# Revit family: Rohrschelle Maxima PSM, M10-M12, Ø 65-117, Gummi
name_source: partatom
category: HLS-Bauteile
revit_build: Autodesk Revit 2017 (Build: 20190507_1515(x64)
units: mm (PartAtom-declared; Revit-internal decimal feet)

## family parameters
Arbeitsebenenbasiert = Ja
Beim Laden mit Abzugskörper schneiden = Nein
Bemaßung runder Anschluss = Durchmesser verwenden
Gemeinsam genutzt = Ja
Immer vertikal = Nein
Raumberechnungspunkt = Nein
Teiletyp = Normal

## types (7) — shared parameters
A = 31 mm  [stored 0.101706 ft]
Anschluss = M10/M12
Anschlußhöhe = 30 mm
Bauart = zweiteilig
Baustoffklasse = B2
Brandschutz = RAL-GZ 656
DF1 = 26 mm  [stored 0.0853018 ft]
DF2 = 28 mm  [stored 0.0918635 ft]
DS = 6 mm  [stored 0.019685 ft]
DVS = 15 mm  [stored 0.0492126 ft]
Dämmstärke = 6 mm  [stored 0.019685 ft]
Fabrikat = MEFA
Farbe Schalldämmeinlage = schwarz
Firma = MEFA Befestigungs- und Montagesysteme GmbH
HGA = 22 mm  [stored 0.0721785 ft]
Kurztext1 = Rohrschelle Maxima PSM 30x3,0
MB = 30 mm  [stored 0.0984252 ft]
MD = 3 mm  [stored 0.00984252 ft]
Material = Stahl
Material Schalldämmeinlage = TPE
Materialmaße = 30x3,0 mm
Materialname = S235
Mengeneinheit = St
Oberflaeche = galvanisch verzinkt
Schalldämmeinlage = Gummi
Verschluss-Schraube = M8
Vorgabe-Ansicht = 1219 mm
max. Temperaturbeständigkeit = 100 °C
max. zul. Last = 1.70 kN
max. zul. Last horizontal = 0.00 kN
max. zul. Last vertikal = 0.00 kN
zero-valued in all types: Nennweite DN Rohr, Rohraußendurchmesser, Stärke Material

## per-type parameters (varying)
| type | AB | Achsabstand | Artikelnummer | B | Breite | D | D0 | Dmax | Dmin | EAN | Gewicht | Gewicht pro Bauteil | H | Kurztext2 | R | RM | Rohraußendurchmesser Zoll | S | Verschluss | max. Höhe | max. Rohraußendurchmesser | min. Rohraußendurchmesser | vpe |
| Maxima PSM, M10/M12, Ø 65- 70, Gummi | 5 mm  [stored 0.0164042 ft] | 116 mm | 008007501 | 142 mm | 142 mm | 70 mm  [stored 0.229659 ft] | 82 mm  [stored 0.269029 ft] | 70 mm  [stored 0.229659 ft] | 65 mm  [stored 0.213255 ft] | 4250928454812 | 0.38 kg | 0.38 kg | 110 mm | 65 - 70 mm M10/M12 TPE | 41 mm  [stored 0.134514 ft] | 44 mm |  | 116 mm | Pendelsteckmutter | 109 mm  [stored 0.357612 ft] | 70 mm  [stored 0.229659 ft] | 65 mm  [stored 0.213255 ft] | St |
| Maxima PSM, M10/M12, Ø 72- 78, Gummi | 6 mm  [stored 0.019685 ft] | 124 mm | 008010601 | 150 mm | 150 mm | 78 mm  [stored 0.255906 ft] | 90 mm  [stored 0.295276 ft] | 78 mm  [stored 0.255906 ft] | 72 mm  [stored 0.23622 ft] | 4250928454829 | 0.40 kg | 0.40 kg | 118 mm  [stored 0.387139 ft] | 72 - 78 mm M10/M12 TPE | 45 mm  [stored 0.147638 ft] | 48 mm  [stored 0.15748 ft] | 2 1/2 Zoll | 124 mm | Pendelsteckmuttern | 117 mm  [stored 0.383858 ft] | 78 mm  [stored 0.255906 ft] | 72 mm  [stored 0.23622 ft] | 1 St |
| Maxima PSM, M10/M12, Ø 84- 90, Gummi | 6 mm  [stored 0.019685 ft] | 136 mm | 008010701 | 162 mm | 162 mm | 90 mm  [stored 0.295276 ft] | 102 mm  [stored 0.334646 ft] | 90 mm  [stored 0.295276 ft] | 84 mm  [stored 0.275591 ft] | 4250928454836 | 0.43 kg | 0.43 kg | 130 mm | 84 - 90 mm M10/M12 TPE | 51 mm  [stored 0.167323 ft] | 54 mm  [stored 0.177165 ft] | 3 Zoll | 136 mm | Pendelsteckmuttern | 129 mm | 90 mm  [stored 0.295276 ft] | 84 mm  [stored 0.275591 ft] | 1 St |
| Maxima PSM, M10/M12, Ø 94-100, Gummi | 6 mm  [stored 0.019685 ft] | 146 mm | 008010801 | 172 mm | 172 mm | 100 mm  [stored 0.328084 ft] | 112 mm  [stored 0.367454 ft] | 100 mm  [stored 0.328084 ft] | 94 mm  [stored 0.308399 ft] | 4250928454843 | 0.46 kg | 0.46 kg | 140 mm | 94 - 100 mm M10/M12 TPE | 56 mm  [stored 0.183727 ft] | 59 mm  [stored 0.19357 ft] | Zoll | 146 mm | Pendelsteckmuttern | 139 mm | 100 mm  [stored 0.328084 ft] | 94 mm  [stored 0.308399 ft] | 1 St |
| Maxima PSM, M10/M12, Ø102-106, Gummi | 4 mm  [stored 0.0131234 ft] | 152 mm | 008014801 | 178 mm | 178 mm | 106 mm  [stored 0.347769 ft] | 118 mm  [stored 0.387139 ft] | 106 mm  [stored 0.347769 ft] | 102 mm  [stored 0.334646 ft] | 4250928454850 | 0.49 kg | 0.49 kg | 146 mm | 102 - 106 mm M10/M12 TPE | 59 mm  [stored 0.19357 ft] | 62 mm  [stored 0.203412 ft] | Zoll | 152 mm | Pendelsteckmuttern | 145 mm | 106 mm  [stored 0.347769 ft] | 102 mm  [stored 0.334646 ft] | 1 St |
| Maxima PSM, M10/M12, Ø108-112, Gummi | 4 mm  [stored 0.0131234 ft] | 158 mm | 008015901 | 184 mm | 184 mm | 112 mm  [stored 0.367454 ft] | 124 mm | 112 mm  [stored 0.367454 ft] | 108 mm  [stored 0.354331 ft] | 4250928454867 | 0.51 kg | 0.51 kg | 152 mm | 108 - 112 mm M10/M12 TPE | 62 mm  [stored 0.203412 ft] | 65 mm  [stored 0.213255 ft] | Zoll | 158 mm | Pendelsteckmuttern | 151 mm | 112 mm  [stored 0.367454 ft] | 108 mm  [stored 0.354331 ft] | 1 St |
| Maxima PSM, M10/M12, Ø113-117, Gummi | 4 mm  [stored 0.0131234 ft] | 168 mm | 008016701 | 189 mm | 189 mm | 117 mm  [stored 0.383858 ft] | 129 mm | 117 mm  [stored 0.383858 ft] | 113 mm  [stored 0.370735 ft] | 4250928455321 | 0.52 kg | 0.52 kg | 157 mm | 113 - 117 mm M10/M12 TPE | 65 mm  [stored 0.213255 ft] | 68 mm | 4 Zoll | 163 mm | Pendelsteckmuttern | 156 mm | 117 mm  [stored 0.383858 ft] | 113 mm  [stored 0.370735 ft] | 1 St |

note: [stored X ft] marks values corroborated as IEEE doubles in the binary element streams (Revit-internal decimal feet)

## geometry (parser evidence)
native form markers: Sweep x4
no freeform markers — native parametric forms only
